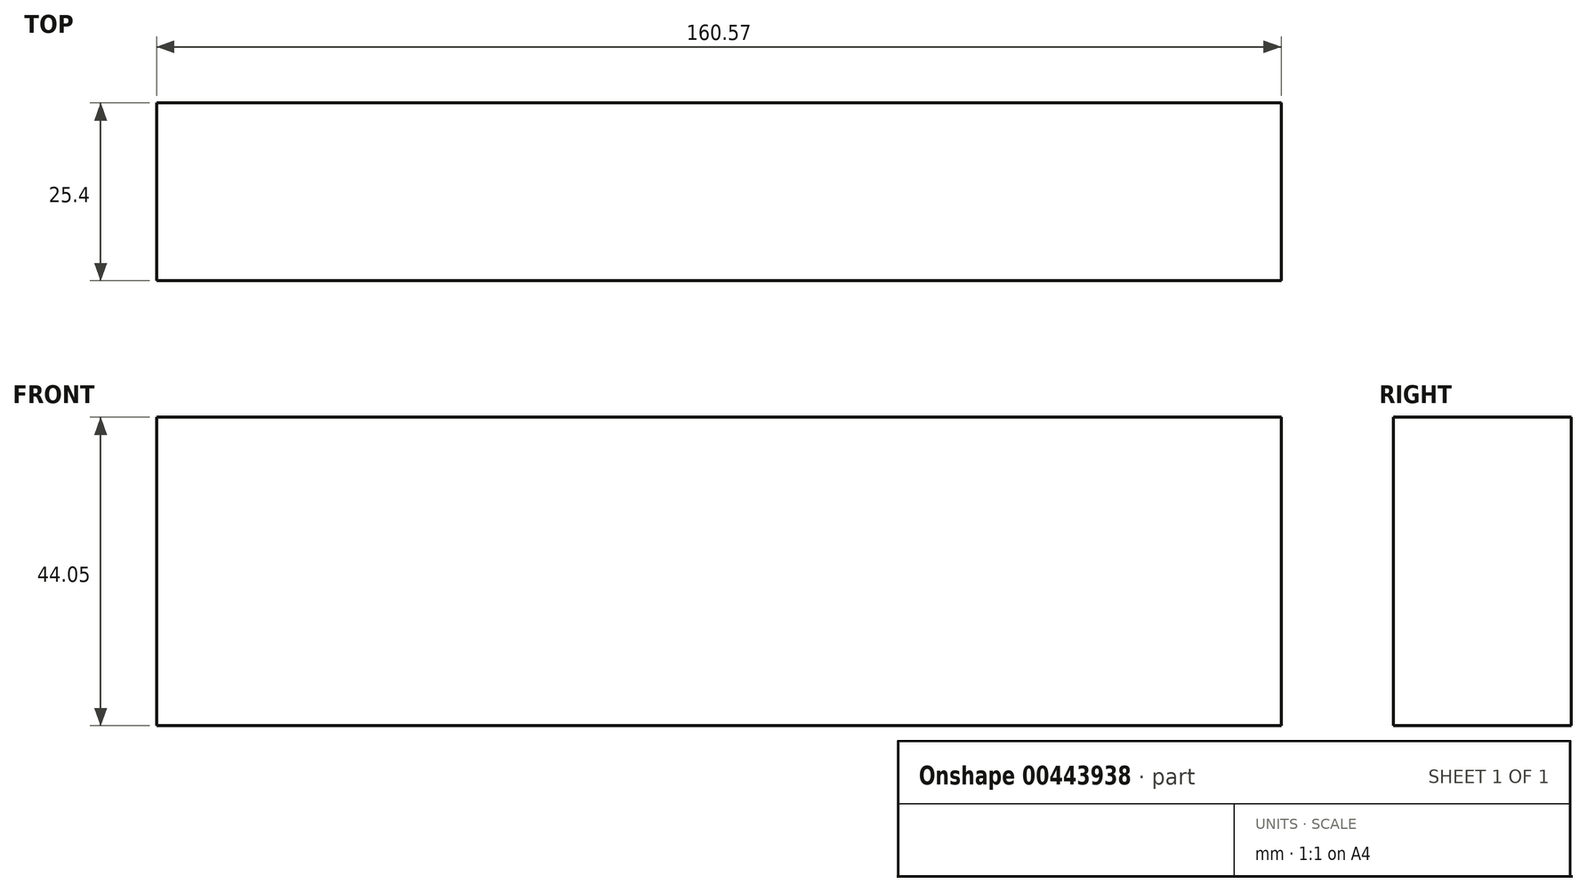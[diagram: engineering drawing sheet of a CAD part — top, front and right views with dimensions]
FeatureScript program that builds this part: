
annotation { "Feature Type Name" : "Feature", "Feature Type Description" : "" }
export const myFeature = defineFeature(function(context is Context, id is Id, definition is map)
    precondition{}
    {
        {
            var Q0;
            Q0=qCreatedBy(makeId("Front.planeOp"),FACE);
            var sketch = newSketch(context, id + "F0", { "sketchPlane" : qUnion([Q0])});
            skLineSegment(sketch, "E0.bottom", {"start": v(-64.13, 44.05) * mm, "end": v(96.44, 44.05) * mm});
            skLineSegment(sketch, "E0.top", {"start": v(-64.13, 0) * mm, "end": v(96.44, 0) * mm});
            skLineSegment(sketch, "E0.left", {"start": v(-64.13, 44.05) * mm, "end": v(-64.13, 0) * mm});
            skLineSegment(sketch, "E0.right", {"start": v(96.44, 44.05) * mm, "end": v(96.44, 0) * mm});
            skLineSegment(sketch, "E1.bottom", {"start": v(96.44, 44.05) * mm, "end": v(-64.13, 44.05) * mm});
            skLineSegment(sketch, "E1.top", {"start": v(96.44, 44.05) * mm, "end": v(-64.13, 44.05) * mm});
            skLineSegment(sketch, "E1.left", {"start": v(96.44, 44.05) * mm, "end": v(96.44, 44.05) * mm});
            skLineSegment(sketch, "E1.right", {"start": v(-64.13, 44.05) * mm, "end": v(-64.13, 44.05) * mm});
            skSolve(sketch);
        }
        {
            var Q0;
            Q0=makeQuery(id+"F0.imprint","IMPRINT",FACE,{"disambiguationData":[TD([[makeQuery(id+"F0.imprint","IMPRINT",EDGE,{"derivedFrom":sQuery(id+"F0.wireOp",EDGE,"E0.top")}),1.0]])]});
            var sketch = newSketch(context, id + "F1", { "sketchPlane" : qUnion([Q0])});
            skSolve(sketch);
        }
        {
            var Q0;
            Q0 = qSketchRegion(id + "F1", true);
            var Q1;
            Q1=makeQuery(id+"F0.imprint","IMPRINT",FACE,{"disambiguationData":[TD([[makeQuery(id+"F0.imprint","IMPRINT",EDGE,{"derivedFrom":sQuery(id+"F0.wireOp",EDGE,"E0.top")}),1.0]])]});
            extrude(context, id + "F2", {"entities" : qUnion([Q0, Q1]), "depth" : 25.4 * mm});
        }
    });
